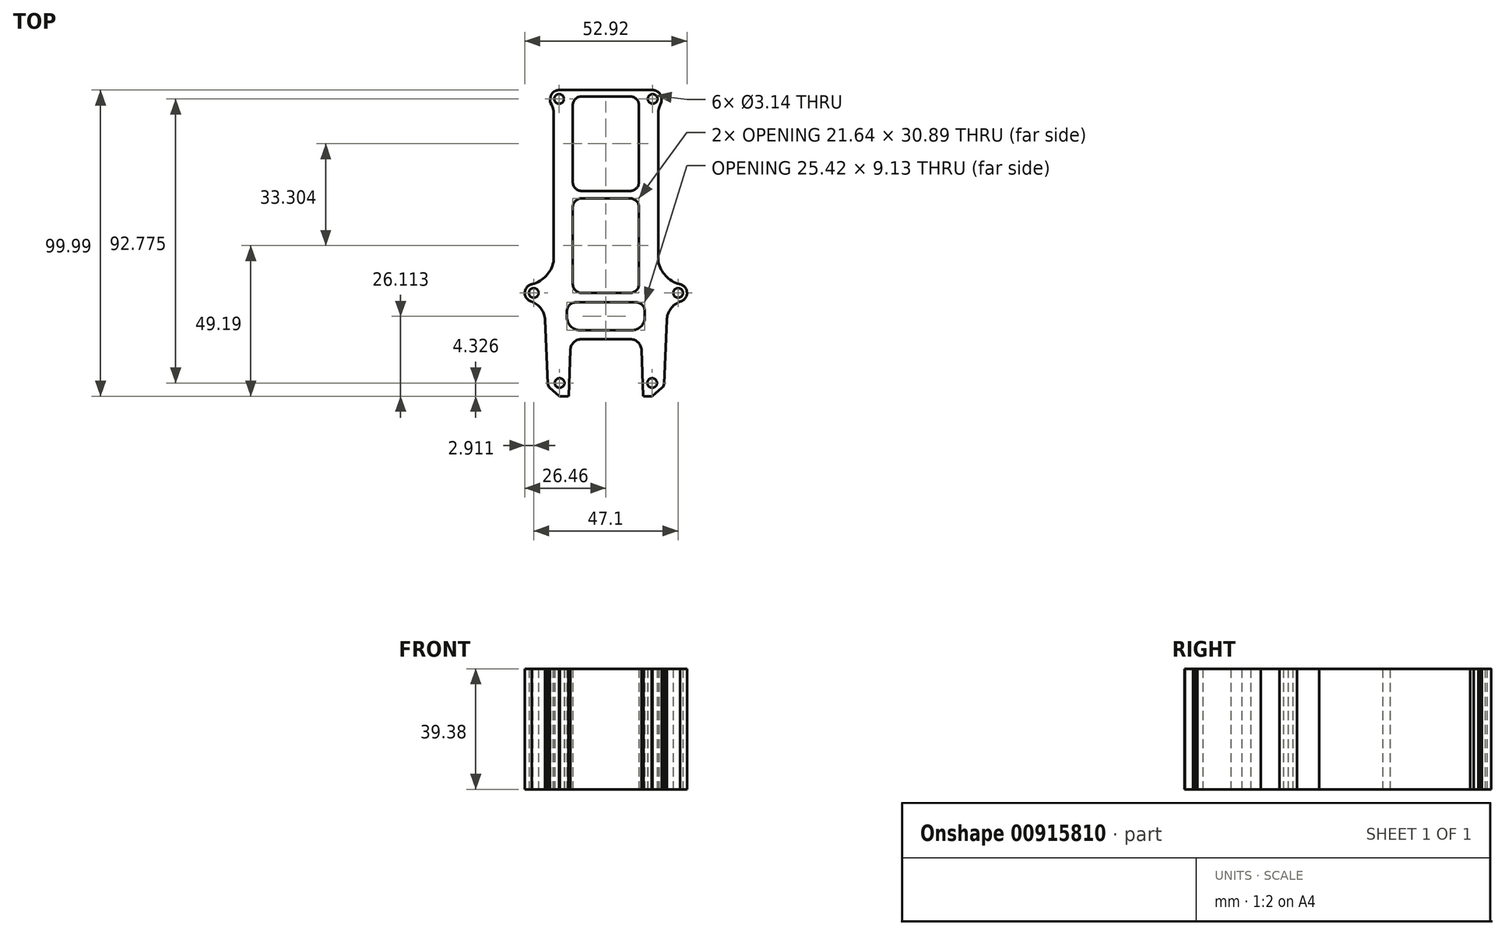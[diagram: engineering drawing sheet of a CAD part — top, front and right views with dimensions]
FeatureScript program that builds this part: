
annotation { "Feature Type Name" : "Feature", "Feature Type Description" : "" }
export const myFeature = defineFeature(function(context is Context, id is Id, definition is map)
    precondition{}
    {
        {
            var Q0;
            Q0=qCreatedBy(makeId("Top.planeOp"),FACE);
            var sketch = newSketch(context, id + "F0", { "sketchPlane" : qUnion([Q0])});
            skLineSegment(sketch, "E0.left", {"start": v(-27.58, 80.06) * mm, "end": v(-27.58, 5.3) * mm});
            skLineSegment(sketch, "E1.bottom", {"start": v(-11.99, 35.27) * mm, "end": v(1.51, 35.27) * mm});
            skLineSegment(sketch, "E1.top", {"start": v(-11.99, -8.8) * mm, "end": v(1.51, -8.8) * mm});
            skLineSegment(sketch, "E1.left", {"start": v(-14.99, 32.27) * mm, "end": v(-14.99, -5.8) * mm});
            skPoint(sketch, "E2.visualSharp", {"position": v(-14.99, 36.07) * mm});
            skArc(sketch, "E2.filletArc", {"start": v(-11.99, 35.27) * mm, "mid": v(-14.1, 34.39) * mm, "end": v(-14.99, 32.27) * mm});
            skPoint(sketch, "E3.visualSharp", {"position": v(-14.99, -8.8) * mm});
            skArc(sketch, "E3.filletArc", {"start": v(-14.99, -5.8) * mm, "mid": v(-14.1, -7.92) * mm, "end": v(-11.99, -8.8) * mm});
            skLineSegment(sketch, "E4.bottom", {"start": v(-11.99, 86.01) * mm, "end": v(1.51, 86.01) * mm});
            skLineSegment(sketch, "E4.top", {"start": v(-11.99, 41.94) * mm, "end": v(1.51, 41.94) * mm});
            skLineSegment(sketch, "E4.left", {"start": v(-14.99, 83.01) * mm, "end": v(-14.99, 44.94) * mm});
            skPoint(sketch, "E5.visualSharp", {"position": v(-14.99, 86.01) * mm});
            skArc(sketch, "E5.filletArc", {"start": v(-11.99, 86.01) * mm, "mid": v(-14.1, 85.13) * mm, "end": v(-14.99, 83.01) * mm});
            skPoint(sketch, "E6.visualSharp", {"position": v(-14.99, 41.94) * mm});
            skArc(sketch, "E6.filletArc", {"start": v(-14.99, 44.94) * mm, "mid": v(-14.1, 42.82) * mm, "end": v(-11.99, 41.94) * mm});
            skLineSegment(sketch, "E7.bottom", {"start": v(-12.87, -27.38) * mm, "end": v(1.51, -27.38) * mm});
            skLineSegment(sketch, "E7.top", {"start": v(-14.87, -16.48) * mm, "end": v(1.51, -16.48) * mm});
            skLineSegment(sketch, "E7.left", {"start": v(-17.87, -22.38) * mm, "end": v(-17.87, -19.48) * mm});
            skPoint(sketch, "E8.visualSharp", {"position": v(-17.87, -16.48) * mm});
            skArc(sketch, "E8.filletArc", {"start": v(-14.87, -16.48) * mm, "mid": v(-16.99, -17.36) * mm, "end": v(-17.87, -19.48) * mm});
            skPoint(sketch, "E9.visualSharp", {"position": v(-17.87, -27.38) * mm});
            skArc(sketch, "E9.filletArc", {"start": v(-17.87, -22.38) * mm, "mid": v(-16.4, -25.92) * mm, "end": v(-12.87, -27.38) * mm});
            skLineSegment(sketch, "E10.bottom", {"start": v(-12.18, -34.84) * mm, "end": v(1.51, -34.84) * mm});
            skPoint(sketch, "E11.visualSharp", {"position": v(-16.18, -34.84) * mm});
            skArc(sketch, "E11.filletArc", {"start": v(-12.18, -34.84) * mm, "mid": v(-15, -36.01) * mm, "end": v(-16.18, -38.84) * mm});
            skLineSegment(sketch, "E12", {"start": v(-16.18, -38.84) * mm, "end": v(-16.96, -62.01) * mm});
            skLineSegment(sketch, "E13", {"start": v(-16.96, -62.01) * mm, "end": v(-17.99, -63.22) * mm});
            skLineSegment(sketch, "E14", {"start": v(-17.99, -63.22) * mm, "end": v(-23, -63.22) * mm});
            skLineSegment(sketch, "E15", {"start": v(-23, -63.22) * mm, "end": v(-23.9, -63.02) * mm});
            skLineSegment(sketch, "E16", {"start": v(-23.9, -63.02) * mm, "end": v(-28.85, -58.61) * mm});
            skCircle(sketch, "E17", {"center": v(-23.01, -55.13) * mm, "radius": 2.4 * mm});
            skArc(sketch, "E18", {"start": v(-36.79, -4.43) * mm, "mid": v(-41.81, -10) * mm, "end": v(-37.36, -16.05) * mm});
            skCircle(sketch, "E19", {"center": v(-35.88, -10.3) * mm, "radius": 2.4 * mm});
            skLineSegment(sketch, "E20", {"start": v(-31.78, -23.86) * mm, "end": v(-30.39, -55.6) * mm});
            skLineSegment(sketch, "E21", {"start": v(-30.39, -55.6) * mm, "end": v(-30.18, -56.73) * mm});
            skLineSegment(sketch, "E22", {"start": v(-30.18, -56.73) * mm, "end": v(-29.54, -57.98) * mm});
            skArc(sketch, "E23", {"start": v(-31.78, -23.86) * mm, "mid": v(-33.38, -19.1) * mm, "end": v(-37.36, -16.05) * mm});
            skArc(sketch, "E24", {"start": v(-36.79, -4.43) * mm, "mid": v(-30.84, -0.84) * mm, "end": v(-27.58, 5.3) * mm});
            skCircle(sketch, "E25", {"center": v(-23.25, 86.23) * mm, "radius": 2.4 * mm});
            skArc(sketch, "E26", {"start": v(-23.2, 92.14) * mm, "mid": v(-27.49, 90.34) * mm, "end": v(-29.15, 86) * mm});
            skLineSegment(sketch, "E27", {"start": v(-29.15, 86) * mm, "end": v(-29.15, 84.6) * mm});
            skLineSegment(sketch, "E28", {"start": v(-29.15, 84.6) * mm, "end": v(-28.88, 83.73) * mm});
            skLineSegment(sketch, "E29", {"start": v(-28.88, 83.73) * mm, "end": v(-28.4, 82.67) * mm});
            skLineSegment(sketch, "E30", {"start": v(-28.4, 82.67) * mm, "end": v(-27.86, 81.45) * mm});
            skLineSegment(sketch, "E31", {"start": v(-27.86, 81.45) * mm, "end": v(-27.58, 80.06) * mm});
            skLineSegment(sketch, "E32", {"start": v(-23.2, 92.14) * mm, "end": v(1.51, 92.14) * mm});
            skPoint(sketch, "E33.startSnap0", {"position": v(0.34, 86.01) * mm});
            skLineSegment(sketch, "E34.right", {"start": v(1.51, 92.14) * mm, "end": v(1.51, 86.01) * mm});
            skLineSegment(sketch, "E35.trimOffspring", {"start": v(1.51, 41.94) * mm, "end": v(1.51, 35.27) * mm});
            skLineSegment(sketch, "E36.trimOffspring", {"start": v(1.51, -8.8) * mm, "end": v(1.51, -16.48) * mm});
            skLineSegment(sketch, "E37.trimOffspring", {"start": v(1.51, -27.38) * mm, "end": v(1.51, -34.84) * mm});
            skLineSegment(sketch, "E38", {"start": v(-29.54, -57.98) * mm, "end": v(-28.85, -58.61) * mm});
            skLineSegment(sketch, "E39.0", {"start": v(-26.43, 81.9) * mm, "end": v(-26.08, 80.22) * mm});
            skLineSegment(sketch, "E39.1", {"start": v(-27.04, 83.28) * mm, "end": v(-26.43, 81.9) * mm});
            skLineSegment(sketch, "E39.2", {"start": v(-27.47, 84.26) * mm, "end": v(-27.04, 83.28) * mm});
            skLineSegment(sketch, "E39.3", {"start": v(-27.65, 84.82) * mm, "end": v(-27.47, 84.26) * mm});
            skLineSegment(sketch, "E39.4", {"start": v(-27.65, 86.04) * mm, "end": v(-27.65, 84.82) * mm});
            skArc(sketch, "E39.5", {"start": v(-23.21, 90.64) * mm, "mid": v(-26.42, 89.29) * mm, "end": v(-27.65, 86.04) * mm});
            skLineSegment(sketch, "E39.6", {"start": v(-23.21, 90.64) * mm, "end": v(0.01, 90.64) * mm});
            skLineSegment(sketch, "E39.7", {"start": v(0.01, 90.64) * mm, "end": v(0.01, 87.51) * mm});
            skLineSegment(sketch, "E39.8", {"start": v(-11.99, 87.51) * mm, "end": v(0.01, 87.51) * mm});
            skArc(sketch, "E39.9", {"start": v(-11.99, 87.51) * mm, "mid": v(-15.17, 86.2) * mm, "end": v(-16.49, 83.01) * mm});
            skLineSegment(sketch, "E39.10", {"start": v(-16.49, 83.01) * mm, "end": v(-16.49, 44.94) * mm});
            skLineSegment(sketch, "E39.11", {"start": v(-26.08, 80.22) * mm, "end": v(-26.08, 5.14) * mm});
            skArc(sketch, "E39.12", {"start": v(-16.49, 44.94) * mm, "mid": v(-15.17, 41.76) * mm, "end": v(-11.99, 40.44) * mm});
            skLineSegment(sketch, "E39.13", {"start": v(-11.99, 40.44) * mm, "end": v(0.01, 40.44) * mm});
            skLineSegment(sketch, "E39.14", {"start": v(0.01, 40.44) * mm, "end": v(0.01, 36.77) * mm});
            skLineSegment(sketch, "E39.15", {"start": v(-11.99, 36.77) * mm, "end": v(0.01, 36.77) * mm});
            skArc(sketch, "E39.16", {"start": v(-11.99, 36.77) * mm, "mid": v(-15.17, 35.45) * mm, "end": v(-16.49, 32.27) * mm});
            skLineSegment(sketch, "E39.17", {"start": v(-16.49, 32.27) * mm, "end": v(-16.49, -5.8) * mm});
            skArc(sketch, "E39.18", {"start": v(-16.49, -5.8) * mm, "mid": v(-15.17, -8.98) * mm, "end": v(-11.99, -10.3) * mm});
            skLineSegment(sketch, "E39.19", {"start": v(-18.68, -61.72) * mm, "end": v(-22.84, -61.72) * mm});
            skLineSegment(sketch, "E39.20", {"start": v(-22.84, -61.72) * mm, "end": v(-23.2, -61.64) * mm});
            skLineSegment(sketch, "E39.21", {"start": v(-23.2, -61.64) * mm, "end": v(-27.84, -57.5) * mm});
            skLineSegment(sketch, "E39.22", {"start": v(-28.33, -57.06) * mm, "end": v(-27.84, -57.5) * mm});
            skLineSegment(sketch, "E39.23", {"start": v(-28.74, -56.24) * mm, "end": v(-28.33, -57.06) * mm});
            skLineSegment(sketch, "E39.24", {"start": v(-28.9, -55.44) * mm, "end": v(-28.74, -56.24) * mm});
            skArc(sketch, "E39.25", {"start": v(-36.48, -5.9) * mm, "mid": v(-29.73, -1.85) * mm, "end": v(-26.08, 5.14) * mm});
            skArc(sketch, "E39.26", {"start": v(-36.48, -5.9) * mm, "mid": v(-40.32, -10.08) * mm, "end": v(-36.91, -14.62) * mm});
            skArc(sketch, "E39.27", {"start": v(-30.28, -23.8) * mm, "mid": v(-32.2, -18.2) * mm, "end": v(-36.91, -14.62) * mm});
            skLineSegment(sketch, "E39.28", {"start": v(-30.28, -23.8) * mm, "end": v(-28.9, -55.44) * mm});
            skLineSegment(sketch, "E39.29", {"start": v(-18.44, -61.44) * mm, "end": v(-18.68, -61.72) * mm});
            skLineSegment(sketch, "E39.30", {"start": v(-17.68, -38.81) * mm, "end": v(-18.44, -61.44) * mm});
            skArc(sketch, "E39.31", {"start": v(-12.18, -33.34) * mm, "mid": v(-16.05, -34.94) * mm, "end": v(-17.68, -38.81) * mm});
            skLineSegment(sketch, "E39.32", {"start": v(-12.18, -33.34) * mm, "end": v(0.01, -33.34) * mm});
            skLineSegment(sketch, "E39.33", {"start": v(0.01, -28.88) * mm, "end": v(0.01, -33.34) * mm});
            skLineSegment(sketch, "E39.34", {"start": v(-12.87, -28.88) * mm, "end": v(0.01, -28.88) * mm});
            skArc(sketch, "E39.35", {"start": v(-19.37, -22.38) * mm, "mid": v(-17.46, -26.98) * mm, "end": v(-12.87, -28.88) * mm});
            skLineSegment(sketch, "E39.36", {"start": v(-19.37, -22.38) * mm, "end": v(-19.37, -19.48) * mm});
            skArc(sketch, "E39.37", {"start": v(-14.87, -14.98) * mm, "mid": v(-18.05, -16.3) * mm, "end": v(-19.37, -19.48) * mm});
            skLineSegment(sketch, "E39.38", {"start": v(-14.87, -14.98) * mm, "end": v(0.01, -14.98) * mm});
            skLineSegment(sketch, "E39.39", {"start": v(0.01, -10.3) * mm, "end": v(0.01, -14.98) * mm});
            skLineSegment(sketch, "E39.40", {"start": v(-11.99, -10.3) * mm, "end": v(0.01, -10.3) * mm});
            skSolve(sketch);
        }
        {
            var Q0;
            Q0=makeQuery(id+"F0.imprint","IMPRINT",FACE,{"disambiguationData":[TD([[makeQuery(id+"F0.imprint","IMPRINT",EDGE,{"derivedFrom":sQuery(id+"F0.wireOp",EDGE,"E17")}),-1.0]])]});
            extrude(context, id + "F1", {"entities" : qUnion([Q0]), "depth" : 60 * mm, "offsetDistance" : 25 * mm});
        }
        {
            var Q0;
            Q0=makeQuery(id+"F1.opExtrude","SWEPT_BODY",BODY,{"disambiguationData":[OSD([sQuery(id+"F0.wireOp",EDGE,"E0.left"),sQuery(id+"F0.wireOp",EDGE,"E1.bottom"),sQuery(id+"F0.wireOp",EDGE,"E1.top"),sQuery(id+"F0.wireOp",EDGE,"E1.left"),sQuery(id+"F0.wireOp",EDGE,"E2.filletArc"),sQuery(id+"F0.wireOp",EDGE,"E3.filletArc"),sQuery(id+"F0.wireOp",EDGE,"E4.bottom"),sQuery(id+"F0.wireOp",EDGE,"E4.top"),sQuery(id+"F0.wireOp",EDGE,"E4.left"),sQuery(id+"F0.wireOp",EDGE,"E5.filletArc"),sQuery(id+"F0.wireOp",EDGE,"E6.filletArc"),sQuery(id+"F0.wireOp",EDGE,"E7.bottom"),sQuery(id+"F0.wireOp",EDGE,"E7.top"),sQuery(id+"F0.wireOp",EDGE,"E7.left"),sQuery(id+"F0.wireOp",EDGE,"E8.filletArc"),sQuery(id+"F0.wireOp",EDGE,"E9.filletArc"),sQuery(id+"F0.wireOp",EDGE,"E10.bottom"),sQuery(id+"F0.wireOp",EDGE,"E11.filletArc"),sQuery(id+"F0.wireOp",EDGE,"E12"),sQuery(id+"F0.wireOp",EDGE,"E13"),sQuery(id+"F0.wireOp",EDGE,"E14"),sQuery(id+"F0.wireOp",EDGE,"E15"),sQuery(id+"F0.wireOp",EDGE,"E16"),sQuery(id+"F0.wireOp",EDGE,"E17"),sQuery(id+"F0.wireOp",EDGE,"E18"),sQuery(id+"F0.wireOp",EDGE,"E19"),sQuery(id+"F0.wireOp",EDGE,"E20"),sQuery(id+"F0.wireOp",EDGE,"E21"),sQuery(id+"F0.wireOp",EDGE,"E22"),sQuery(id+"F0.wireOp",EDGE,"649mTeg2-WbHY-aIMV-LATB-YzIlmNDvRgrl"),sQuery(id+"F0.wireOp",EDGE,"E23"),sQuery(id+"F0.wireOp",EDGE,"E24"),sQuery(id+"F0.wireOp",EDGE,"E25"),sQuery(id+"F0.wireOp",EDGE,"E26"),sQuery(id+"F0.wireOp",EDGE,"E27"),sQuery(id+"F0.wireOp",EDGE,"E28"),sQuery(id+"F0.wireOp",EDGE,"E29"),sQuery(id+"F0.wireOp",EDGE,"E30"),sQuery(id+"F0.wireOp",EDGE,"E31"),sQuery(id+"F0.wireOp",EDGE,"E32"),sQuery(id+"F0.wireOp",EDGE,"E34.right"),sQuery(id+"F0.wireOp",EDGE,"E35.trimOffspring"),sQuery(id+"F0.wireOp",EDGE,"E36.trimOffspring"),sQuery(id+"F0.wireOp",EDGE,"E37.trimOffspring")])]});
            var Q1;
            Q1=qCreatedBy(makeId("Right.planeOp"),FACE);
            mirror(context, id + "F2", {"operationType" : NewBodyOperationType.ADD, "entities" : qUnion([Q0]), "mirrorPlane" : qUnion([Q1])});
        }
        {
            var Q0;
            Q0=makeQuery(id+"F1.opExtrude","SWEPT_BODY",BODY,{"disambiguationData":[OSD([sQuery(id+"F0.wireOp",EDGE,"E0.left"),sQuery(id+"F0.wireOp",EDGE,"E1.bottom"),sQuery(id+"F0.wireOp",EDGE,"E1.top"),sQuery(id+"F0.wireOp",EDGE,"E1.left"),sQuery(id+"F0.wireOp",EDGE,"E2.filletArc"),sQuery(id+"F0.wireOp",EDGE,"E3.filletArc"),sQuery(id+"F0.wireOp",EDGE,"E4.bottom"),sQuery(id+"F0.wireOp",EDGE,"E4.top"),sQuery(id+"F0.wireOp",EDGE,"E4.left"),sQuery(id+"F0.wireOp",EDGE,"E5.filletArc"),sQuery(id+"F0.wireOp",EDGE,"E6.filletArc"),sQuery(id+"F0.wireOp",EDGE,"E7.bottom"),sQuery(id+"F0.wireOp",EDGE,"E7.top"),sQuery(id+"F0.wireOp",EDGE,"E7.left"),sQuery(id+"F0.wireOp",EDGE,"E8.filletArc"),sQuery(id+"F0.wireOp",EDGE,"E9.filletArc"),sQuery(id+"F0.wireOp",EDGE,"E10.bottom"),sQuery(id+"F0.wireOp",EDGE,"E11.filletArc"),sQuery(id+"F0.wireOp",EDGE,"E12"),sQuery(id+"F0.wireOp",EDGE,"E13"),sQuery(id+"F0.wireOp",EDGE,"E14"),sQuery(id+"F0.wireOp",EDGE,"E15"),sQuery(id+"F0.wireOp",EDGE,"E16"),sQuery(id+"F0.wireOp",EDGE,"E17"),sQuery(id+"F0.wireOp",EDGE,"E18"),sQuery(id+"F0.wireOp",EDGE,"E19"),sQuery(id+"F0.wireOp",EDGE,"E20"),sQuery(id+"F0.wireOp",EDGE,"E21"),sQuery(id+"F0.wireOp",EDGE,"E22"),sQuery(id+"F0.wireOp",EDGE,"649mTeg2-WbHY-aIMV-LATB-YzIlmNDvRgrl"),sQuery(id+"F0.wireOp",EDGE,"E23"),sQuery(id+"F0.wireOp",EDGE,"E24"),sQuery(id+"F0.wireOp",EDGE,"E25"),sQuery(id+"F0.wireOp",EDGE,"E26"),sQuery(id+"F0.wireOp",EDGE,"E27"),sQuery(id+"F0.wireOp",EDGE,"E28"),sQuery(id+"F0.wireOp",EDGE,"E29"),sQuery(id+"F0.wireOp",EDGE,"E30"),sQuery(id+"F0.wireOp",EDGE,"E31"),sQuery(id+"F0.wireOp",EDGE,"E32"),sQuery(id+"F0.wireOp",EDGE,"E34.right"),sQuery(id+"F0.wireOp",EDGE,"E35.trimOffspring"),sQuery(id+"F0.wireOp",EDGE,"E36.trimOffspring"),sQuery(id+"F0.wireOp",EDGE,"E37.trimOffspring")])]});
            var Q1;
            Q1=sQuery(id+"F0.wireOp",VERTEX,"E1.top.end");
            transform(context, id + "F3", {"entities" : qUnion([Q0]), "transformType" : TransformType.SCALE_UNIFORMLY, "scale" : 0.66, "scalePoint" : qUnion([Q1]), "makeCopy" : false});
        }
    });
